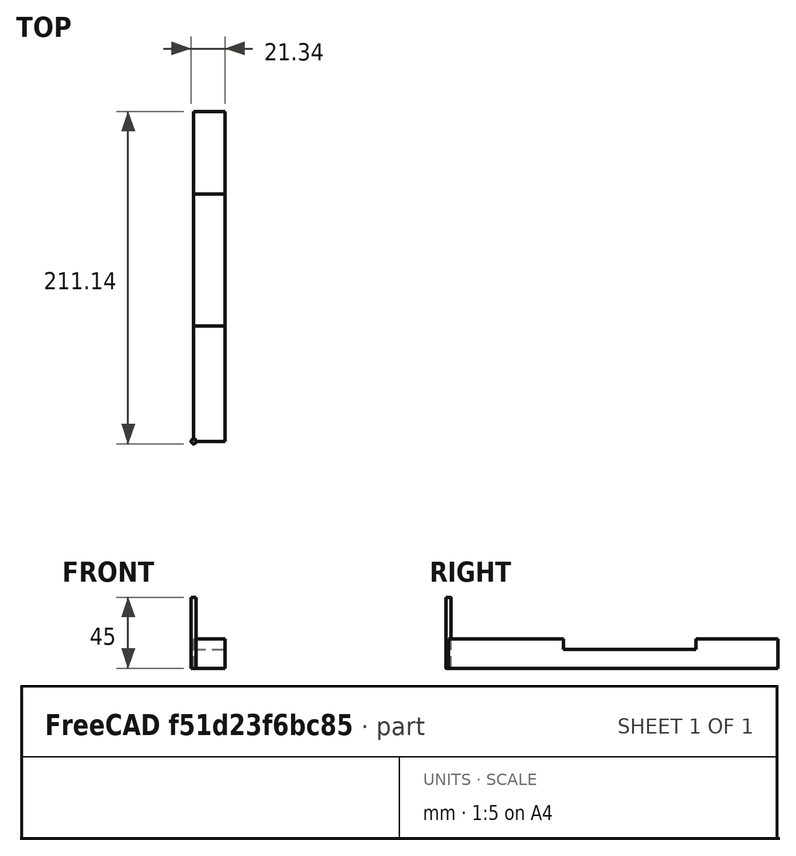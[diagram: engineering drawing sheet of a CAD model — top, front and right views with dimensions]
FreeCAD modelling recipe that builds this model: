
FCSTD DOCUMENT  (FreeCAD 1.1R20251125 (Git shallow))
Label: Frame-Mill-Out
License: All rights reserved
LicenseURL: https://en.wikipedia.org/wiki/All_rights_reserved
objects: App::Point×3, Sketcher::SketchObject×3, Part::FeaturePython×3, App::DocumentObjectGroup×3, Path::FeaturePython×3, PartDesign::Body×2, App::FeaturePython×2, PartDesign::Pad×1, PartDesign::Pocket×1, App::Part×1, PartDesign::Revolution×1, Mesh::FeaturePython×1
note: 21 computed .brp shape members not serialized (recipe doc carries the construction recipe); baked Part::Feature solids carry a one-line shape summary decoded from their .brp

FEATURE [App::Point] Origin001
  Role = Origin
FEATURE [App::Point] Origin003
  Role = Origin
FEATURE [Sketcher::SketchObject] Sketch
  ArcFitTolerance = 1e-06
  AttachmentSupport = -> [Origin002]
  ExternalTypes = [0]
  FullyConstrained = true
  MakeInternals = false
  MapMode = 5
  sketch-geometry (4):
    g0: LineSegment StartX=0 StartY=0 StartZ=0 EndX=19.75 EndY=0 EndZ=0
    g1: LineSegment StartX=19.75 StartY=0 StartZ=0 EndX=19.75 EndY=209.55 EndZ=0
    g2: LineSegment StartX=19.75 StartY=209.55 StartZ=0 EndX=0 EndY=209.55 EndZ=0
    g3: LineSegment StartX=0 StartY=209.55 StartZ=0 EndX=0 EndY=0 EndZ=0
  constraints (11):
    c: Coincident(g0,g1)
    c: Coincident(g1,g2)
    c: Coincident(g2,g3)
    c: Coincident(g3,g0)
    c: Horizontal(g0)
    c: Horizontal(g2)
    c: Vertical(g1)
    c: Vertical(g3)
    c: Distance(g1,g3) = 19.75
    c: Distance(g0,g2) = 209.55
    c: Coincident(g0,g-1)
FEATURE [PartDesign::Pad] Pad
  Direction = (0,0,1)
  Length = 18.5
  Length2 = 10
  Profile = -> Sketch
  ReferenceAxis = -> Sketch [N_Axis]
  Refine = true
  SideType = 0
  Suppressed = false
  Type = 0
  Type2 = 0
FEATURE [Sketcher::SketchObject] Sketch001
  ArcFitTolerance = 1e-06
  AttachmentSupport = -> [Pad]
  ExternalGeometry = -> [Pad]
  ExternalTypes = [0]
  FullyConstrained = false
  MakeInternals = false
  MapMode = 5
  Placement = pos=(0,0,18.5) rot=(0,0,1;0rad)
  sketch-geometry (4):
    g0: LineSegment StartX=-18.2563 StartY=157.2 StartZ=0 EndX=-18.2563 EndY=73.2 EndZ=0
    g1: LineSegment StartX=-18.2563 StartY=73.2 StartZ=0 EndX=31.968 EndY=73.2 EndZ=0
    g2: LineSegment StartX=31.968 StartY=73.2 StartZ=0 EndX=31.968 EndY=157.2 EndZ=0
    g3: LineSegment StartX=31.968 StartY=157.2 StartZ=0 EndX=-18.2563 EndY=157.2 EndZ=0
  constraints (11):
    c: Coincident(g0,g1)
    c: Coincident(g1,g2)
    c: Coincident(g2,g3)
    c: Coincident(g3,g0)
    c: Vertical(g0)
    c: Vertical(g2)
    c: Horizontal(g1)
    c: Horizontal(g3)
    c: Distance(g0,g2) = 50.2243
    c: Distance(g1,g3) = 84
    c: Distance(g-5,g3) = 52.35
FEATURE [PartDesign::Pocket] Pocket
  BaseFeature = -> Pad
  Direction = (0,0,-1)
  Length = 6.5
  Length2 = 5
  Profile = -> Sketch001
  ReferenceAxis = -> Sketch001 [N_Axis]
  Refine = true
  SideType = 0
  Suppressed = false
  Type = 0
  Type2 = 0
FEATURE [PartDesign::Body] Body
  AllowCompound = false
  Group = -> [Sketch,Pad,Sketch001,Pocket]
  Origin = -> Origin002
  Tip = -> Pocket
FEATURE [App::Part] Part  label="Frame-Side"
  Group = -> [Body]
  Origin = -> Origin
FEATURE [App::FeaturePython] SetupSheet  # Path/CAM operation (typed FeaturePython)
  ClearanceHeightExpression = OpStockZMax+SetupSheet.ClearanceHeightOffset
  ClearanceHeightOffset = 5
  CoolantMode = 0
  CoolantModes = None | Flood | Mist
  FinalDepthExpression = OpFinalDepth
  HorizRapid = 0
  SafeHeightExpression = OpStockZMax+SetupSheet.SafeHeightOffset
  SafeHeightOffset = 3
  StartDepthExpression = OpStartDepth
  StepDownExpression = OpToolDiameter
  VertRapid = 0
FEATURE [Part::FeaturePython] Clone  label="Model-Frame-Side"  # Draft clone (typed FeaturePython)
  AttacherType = Attacher::AttachEngine3D
  ForceCompound = false
  Fuse = false
  Objects = -> [Part]
  PathResource = Model
  Placement = pos=(3.5e-15,15.75,-18.5) rot=(0,0,1;4.71239rad)
  Scale = (1,1,1)
FEATURE [App::DocumentObjectGroup] Model
  Group = -> [Clone]
FEATURE [App::FeaturePython] PropertyBag001  label="Attributes001"  # WARN: FeaturePython — macro-defined, semantics opaque (R4)
  CustomPropertyGroups = 0
  CuttingEdgeHeight = 25
  Diameter = 3.175
  Flutes = 4
  Length = 45
  ShankDiameter = 3.175
FEATURE [Sketcher::SketchObject] Sketch003
  ArcFitTolerance = 0
  AttachmentSupport = -> [XZ_Plane003]
  ExternalTypes = [0]
  FullyConstrained = true
  MakeInternals = false
  MapMode = 5
  Placement = pos=(0,0,0) rot=(1,0,0;1.5708rad)
  expr: Constraints[10] = <<Attributes001>>.Length
  expr: Constraints[16] = <<Attributes001>>.ShankDiameter
  expr: Constraints[18] = <<Attributes001>>.CuttingEdgeHeight
  expr: Constraints[9] = <<Attributes001>>.Diameter
  sketch-geometry (8):
    g0: LineSegment StartX=0 StartY=45 StartZ=0 EndX=0 EndY=0 EndZ=0
    g1: LineSegment StartX=0 StartY=0 StartZ=0 EndX=1.5875 EndY=0 EndZ=0
    g2: LineSegment StartX=1.5875 StartY=0 StartZ=0 EndX=1.5875 EndY=25 EndZ=0
    g3: LineSegment StartX=1.5875 StartY=45 StartZ=0 EndX=0 EndY=45 EndZ=0
    g4: LineSegment [constr] StartX=1.5875 StartY=0 StartZ=0 EndX=-1.5875 EndY=0 EndZ=0
    g5: LineSegment StartX=1.5875 StartY=24.99 StartZ=0 EndX=1.5875 EndY=25 EndZ=0
    g6: LineSegment StartX=1.5875 StartY=45 StartZ=0 EndX=1.5875 EndY=24.99 EndZ=0
    g7: LineSegment [constr] StartX=-1.5875 StartY=45 StartZ=0 EndX=1.5875 EndY=45 EndZ=0
  constraints (21):
    c: Vertical(g0)
    c: Coincident(g0,g1)
    c: Horizontal(g1)
    c: Coincident(g1,g2)
    c: Vertical(g2)
    c: Horizontal(g3)
    c: Coincident(g0,g3)
    c: Coincident(g4,g1)
    c: Symmetric(g1,g4,g0)
    c: DistanceX(g4,g4) = 3.175
    c: DistanceY(g2,g3) = 45
    c: Coincident(g2,g5)
    c: Vertical(g6)
    c: Coincident(g3,g6)
    c: Symmetric(g7,g7,g0)
    c: Coincident(g7,g3)
    c: DistanceX(g7,g7) = 3.175
    c: Coincident(g5,g6)
    c: DistanceY(g2) = 25
    c: Coincident(g0,g-1)
    c: DistanceY(g5,g2) = 0.01
FEATURE [PartDesign::Revolution] Revolution001
  AllowMultiFace = false
  Angle = 360
  Angle2 = 60
  Axis = (0,2e-16,1)
  Base = (0,0,0)
  Placement = pos=(0,0,0) rot=(1,0,0;1.5708rad)
  Profile = -> Sketch003
  ReferenceAxis = -> Sketch003 [V_Axis]
  Reversed = true
  Suppressed = false
  Type = 0
FEATURE [App::Point] Origin006  label="Origin007"
  Role = Origin
FEATURE [PartDesign::Body] Body002  label="Endmill002"
  AllowCompound = false
  Group = -> [Sketch003,Revolution001,PropertyBag001]
  Origin = -> Origin007
  Tip = -> Revolution001
FEATURE [Part::FeaturePython] _3_175mm_Endmill  label="3.175mm Endmill"  # WARN: FeaturePython — macro-defined, semantics opaque (R4)
  BitBody = -> Body002
  Chipload = 0
  CuttingEdgeHeight = 25
  Diameter = 3.175
  Flutes = 4
  Length = 45
  Material = 0
  ShankDiameter = 3.175
  ShapeID = endmill
  ShapeType = 6
  SpindleDirection = 0
  ToolBitID = 3.175mm_Endmill
FEATURE [Path::FeaturePython] _3_175mm_Endmill001  label="3.175mm Endmill001"  # Path/CAM operation (typed FeaturePython)
  HorizFeed = 10
  HorizRapid = 0
  SpindleDir = 0
  SpindleSpeed = 0
  Tool = -> _3_175mm_Endmill
  ToolNumber = 2
  VertFeed = 10
  VertRapid = 0
  expr: HorizRapid = SetupSheet.HorizRapid
  expr: VertRapid = SetupSheet.VertRapid
FEATURE [App::DocumentObjectGroup] Tools
  Group = -> [_3_175mm_Endmill001]
FEATURE [Path::FeaturePython] Adaptive  # Path/CAM operation (typed FeaturePython)
  Active = true
  Base = -> [Clone]
  ClearanceHeight = 23.5
  CoolantMode = 0
  CycleTime = 00:00:02
  ExtensionCorners = true
  ExtensionLengthDefault = 1.5875
  FinalDepth = 0
  FinishDepth = 0.2
  FinishingProfile = true
  ForceInsideOut = false
  HelixAngle = 5
  HelixConeAngle = 0
  HelixDiameterLimit = 0
  KeepToolDownRatio = 3
  LiftDistance = 0
  ModelAwareExperiment = false
  OpFinalDepth = 0
  OpStartDepth = 18.5
  OpStockZMax = 18.5
  OpStockZMin = 0
  OpToolDiameter = 3.175
  OperationType = 0
  OrderCutsByRegion = false
  SafeHeight = 21.5
  Side = 1
  StartDepth = 18.5
  StepDown = 1
  StepOver = 20
  StockToLeave = 0
  StopProcessing = false
  Stopped = false
  Tolerance = 0.1
  ToolController = -> _3_175mm_Endmill001
  UseHelixArcs = false
  UseOutline = true
  ZStockToLeave = 0
  expr: ClearanceHeight = OpStockZMax + SetupSheet.ClearanceHeightOffset
  expr: ExtensionLengthDefault = OpToolDiameter / 2
  expr: FinalDepth = OpFinalDepth
  expr: SafeHeight = OpStockZMax + SetupSheet.SafeHeightOffset
  expr: StartDepth = OpStartDepth
  expr: StepDown = 1
FEATURE [App::DocumentObjectGroup] Operations
  Group = -> [Adaptive]
FEATURE [Mesh::FeaturePython] CutMaterial  # WARN: FeaturePython — macro-defined, semantics opaque (R4)
FEATURE [Part::FeaturePython] Clone001  label="Stock-Body"  # Draft clone (typed FeaturePython)
  AttacherType = Attacher::AttachEngine3D
  ForceCompound = false
  Fuse = false
  Objects = -> [Body]
  PathResource = Stock
  Scale = (1,1,1)
  StockType = Unknown
FEATURE [Path::FeaturePython] Job  # Path/CAM operation (typed FeaturePython)
  CycleTime = 00:00:02
  Fixtures = G54
  GeometryTolerance = 0.01
  JobType = 0
  Model = -> Model
  Operations = -> Operations
  OrderOutputBy = 0
  PostProcessor = 12
  PostProcessorArgs = --translate_drill
  SetupSheet = -> SetupSheet
  SplitOutput = false
  Stock = -> Clone001
  Tools = -> Tools
